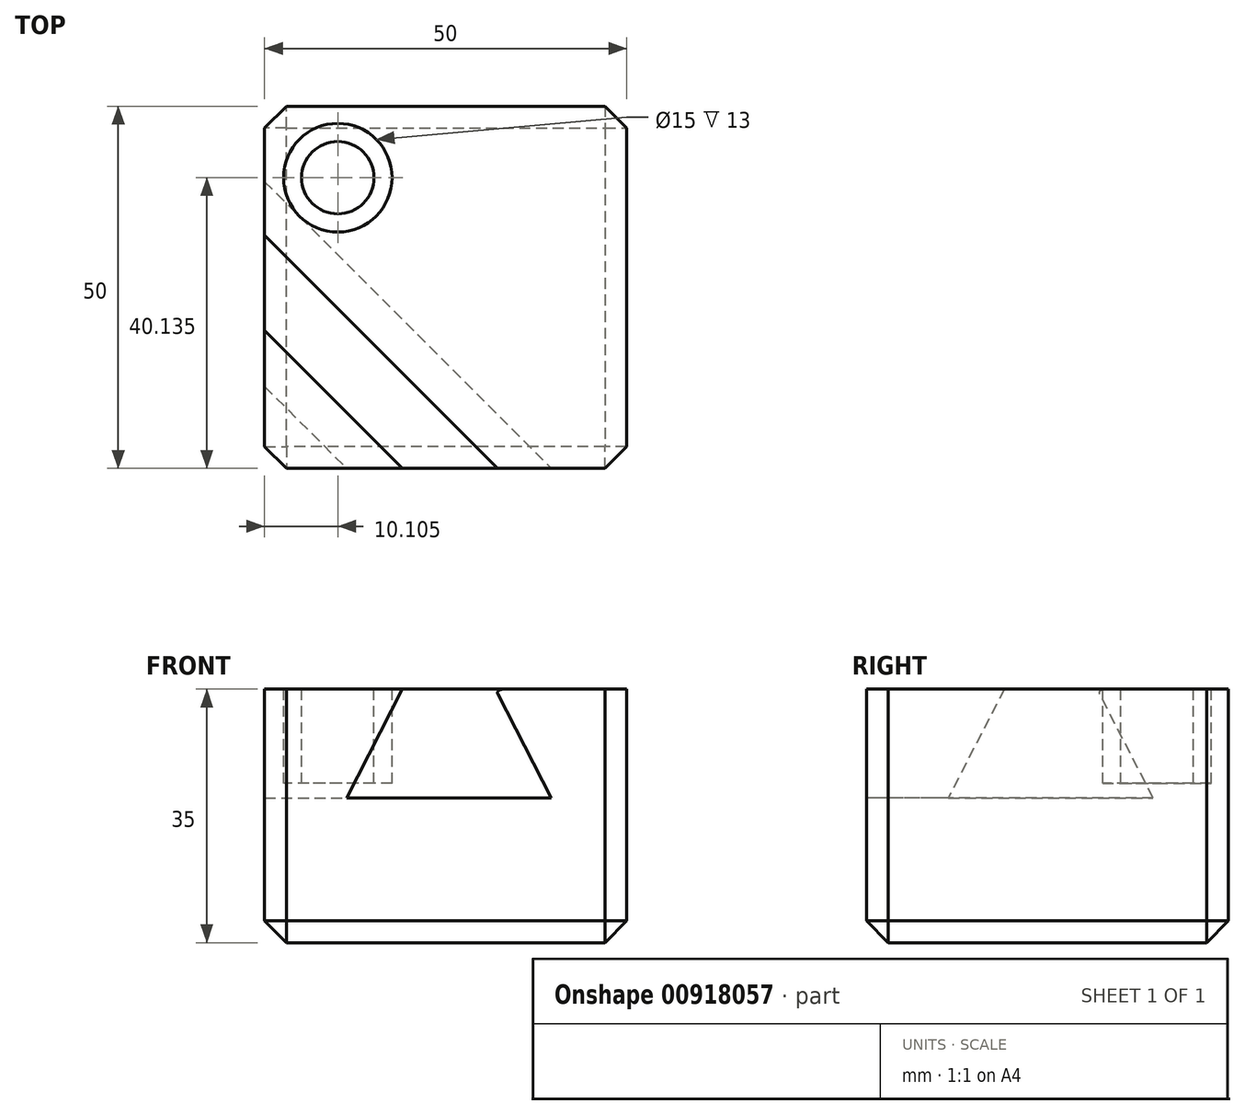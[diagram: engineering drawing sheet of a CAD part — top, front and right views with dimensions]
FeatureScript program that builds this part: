
annotation { "Feature Type Name" : "Feature", "Feature Type Description" : "" }
export const myFeature = defineFeature(function(context is Context, id is Id, definition is map)
    precondition{}
    {
        {
            var Q0;
            Q0=qCreatedBy(makeId("Top.planeOp"),FACE);
            var sketch = newSketch(context, id + "F0", { "sketchPlane" : qUnion([Q0])});
            skLineSegment(sketch, "E0.bottom", {"start": v(25, -25) * mm, "end": v(-25, -25) * mm});
            skLineSegment(sketch, "E0.top", {"start": v(25, 25) * mm, "end": v(-25, 25) * mm});
            skLineSegment(sketch, "E0.left", {"start": v(25, -25) * mm, "end": v(25, 25) * mm});
            skLineSegment(sketch, "E0.right", {"start": v(-25, -25) * mm, "end": v(-25, 25) * mm});
            skPoint(sketch, "E0.middle", {"position": v(0, 0) * mm});
            skSolve(sketch);
        }
        {
            var Q0;
            Q0=qSketchRegion(id+"F0",true);
            extrude(context, id + "F1", {"entities" : qUnion([Q0]), "depth" : 35 * mm, "offsetDistance" : 25 * mm});
        }
        {
            var Q0;
            Q0=makeQuery(id+"F1.opExtrude","SWEPT_EDGE",EDGE,{"disambiguationData":[OSD([sQuery(id+"F0.wireOp",EDGE,"E0.bottom"),sQuery(id+"F0.wireOp",EDGE,"E0.left")])]});
            cPlane(context, id + "F2", {"entities" : qUnion([Q0]), "cplaneType" : CPlaneType.LINE_ANGLE, "offset" : 25 * mm, "angle" : 45 * degree, "width" : 150 * mm, "height" : 150 * mm});
        }
        {
            var Q0;
            Q0=qCreatedBy(id+"F2.planeOp",FACE);
            var sketch = newSketch(context, id + "F3", { "sketchPlane" : qUnion([Q0])});
            skLineSegment(sketch, "E1", {"start": v(21.9, 35) * mm, "end": v(12.81, 35) * mm});
            skLineSegment(sketch, "E2", {"start": v(12.81, 35) * mm, "end": v(7.36, 20) * mm});
            skLineSegment(sketch, "E3", {"start": v(7.36, 20) * mm, "end": v(27.36, 20) * mm});
            skLineSegment(sketch, "E4", {"start": v(27.36, 20) * mm, "end": v(21.9, 35) * mm});
            skSolve(sketch);
        }
        {
            var Q0;
            Q0=qSketchRegion(id+"F3",true);
            extrude(context, id + "F4", {"entities" : qUnion([Q0]), "operationType" : NewBodyOperationType.REMOVE, "depth" : 74.81 * mm, "offsetDistance" : 25 * mm});
        }
        {
            var Q0;
            Q0=makeQuery(id+"F1.opExtrude","SWEPT_EDGE",EDGE,{"disambiguationData":[OSD([sQuery(id+"F0.wireOp",EDGE,"E0.bottom"),sQuery(id+"F0.wireOp",EDGE,"E0.left")])]});
            cPlane(context, id + "F5", {"entities" : qUnion([Q0]), "cplaneType" : CPlaneType.LINE_ANGLE, "offset" : 25 * mm, "angle" : 135 * degree, "width" : 150 * mm, "height" : 150 * mm});
        }
        {
            var Q0;
            Q0=makeQuery(id+"F1.opExtrude","CAP_EDGE",EDGE,{"disambiguationData":[OSD([sQuery(id+"F0.wireOp",EDGE,"E0.left")])],"isStart":true});
            var Q1;
            Q1=makeQuery(id+"F1.opExtrude","CAP_EDGE",EDGE,{"disambiguationData":[OSD([sQuery(id+"F0.wireOp",EDGE,"E0.bottom")])],"isStart":true});
            var Q2;
            Q2=makeQuery(id+"F1.opExtrude","CAP_EDGE",EDGE,{"disambiguationData":[OSD([sQuery(id+"F0.wireOp",EDGE,"E0.right")])],"isStart":true});
            var Q3;
            Q3=makeQuery(id+"F1.opExtrude","CAP_EDGE",EDGE,{"disambiguationData":[OSD([sQuery(id+"F0.wireOp",EDGE,"E0.top")])],"isStart":true});
            var Q4;
            Q4=makeQuery(id+"F1.opExtrude","SWEPT_EDGE",EDGE,{"disambiguationData":[OSD([sQuery(id+"F0.wireOp",EDGE,"E0.bottom"),sQuery(id+"F0.wireOp",EDGE,"E0.left")])]});
            var Q5;
            Q5=makeQuery(id+"F1.opExtrude","SWEPT_EDGE",EDGE,{"disambiguationData":[OSD([sQuery(id+"F0.wireOp",EDGE,"E0.bottom"),sQuery(id+"F0.wireOp",EDGE,"E0.right")])]});
            var Q6;
            Q6=makeQuery(id+"F1.opExtrude","SWEPT_EDGE",EDGE,{"disambiguationData":[OSD([sQuery(id+"F0.wireOp",EDGE,"E0.top"),sQuery(id+"F0.wireOp",EDGE,"E0.right")])]});
            var Q7;
            Q7=makeQuery(id+"F1.opExtrude","SWEPT_EDGE",EDGE,{"disambiguationData":[OSD([sQuery(id+"F0.wireOp",EDGE,"E0.top"),sQuery(id+"F0.wireOp",EDGE,"E0.left")])]});
            chamfer(context, id + "F6", {"entities" : qUnion([Q0, Q1, Q2, Q3, Q4, Q5, Q6, Q7]), "width" : 3 * mm, "tangentPropagation" : true});
        }
        {
            var Q0;
            Q0=makeQuery(id+"F4.boolean.opBoolean","COPY",EDGE,{"derivedFrom":makeQuery(id+"F4.opExtrude","SWEPT_EDGE",EDGE,{"disambiguationData":[OSD([sQuery(id+"F3.wireOp",EDGE,"E1"),sQuery(id+"F3.wireOp",EDGE,"E4")])]})});
            var Q1;
            Q1=makeQuery(id+"F4.boolean.opBoolean","COPY",EDGE,{"derivedFrom":makeQuery(id+"F4.opExtrude","SWEPT_EDGE",EDGE,{"disambiguationData":[OSD([sQuery(id+"F3.wireOp",EDGE,"E1"),sQuery(id+"F3.wireOp",EDGE,"E2")])]})});
            var Q2;
            Q2=makeQuery(id+"F466Z8mKHTBogR3_1.1.F4.boolean.opBoolean","COPY",EDGE,{"derivedFrom":makeQuery(id+"F466Z8mKHTBogR3_1.1.F4.opExtrude","SWEPT_EDGE",EDGE,{"disambiguationData":[OSD([sQuery(id+"F3.wireOp",EDGE,"E1"),sQuery(id+"F3.wireOp",EDGE,"E2")])]})});
            var Q3;
            Q3=makeQuery(id+"F466Z8mKHTBogR3_1.1.F4.boolean.opBoolean","COPY",EDGE,{"derivedFrom":makeQuery(id+"F466Z8mKHTBogR3_1.1.F4.opExtrude","SWEPT_EDGE",EDGE,{"disambiguationData":[OSD([sQuery(id+"F3.wireOp",EDGE,"E1"),sQuery(id+"F3.wireOp",EDGE,"E4")])]})});
            fillet(context, id + "F7", {"entities" : qUnion([Q0, Q1, Q2, Q3]), "radius" : .5 * mm, "tangentPropagation" : true, "allowEdgeOverflow" : false});
        }
        {
            var Q0;
            {var subQ0=sQuery(id+"F0.wireOp",EDGE,"E0.left");var subQ2=sQuery(id+"F0.wireOp",EDGE,"E0.top");var subQ3=makeQuery(id+"F1.opExtrude","SWEPT_FACE",FACE,{"disambiguationData":[OSD([subQ2])]});var subQ4=sQuery(id+"F0.wireOp",EDGE,"E0.right");var subQ6=sQuery(id+"F0.wireOp",EDGE,"E0.bottom");var subQ7=makeQuery(id+"F1.opExtrude","SWEPT_FACE",FACE,{"disambiguationData":[OSD([subQ6])]});Q0=makeQuery(id+"F466Z8mKHTBogR3_1.1.F4.boolean.opBoolean","SPLIT",FACE,{"disambiguationData":[TD([subQ7])],"derivedFrom":makeQuery(id+"F4.boolean.opBoolean","SPLIT",FACE,{"disambiguationData":[TD([subQ3])],"derivedFrom":makeQuery(id+"F1.opExtrude","CAP_FACE",FACE,{"disambiguationData":[OSD([subQ6,subQ2,subQ0,subQ4])],"isStart":false})})});}
            var sketch = newSketch(context, id + "F8", { "sketchPlane" : qUnion([Q0])});
            skCircle(sketch, "E5", {"center": v(-14.9, 15.13) * mm, "radius": 7.5 * mm});
            skCircle(sketch, "E6", {"center": v(-14.9, 15.13) * mm, "radius": 5 * mm});
            skSolve(sketch);
        }
        {
            var Q0;
            Q0=qSketchRegion(id+"F8",true);
            extrude(context, id + "F9", {"entities" : qUnion([Q0]), "operationType" : NewBodyOperationType.REMOVE, "oppositeDirection" : true, "depth" : 13 * mm, "offsetDistance" : 25 * mm});
        }
    });
